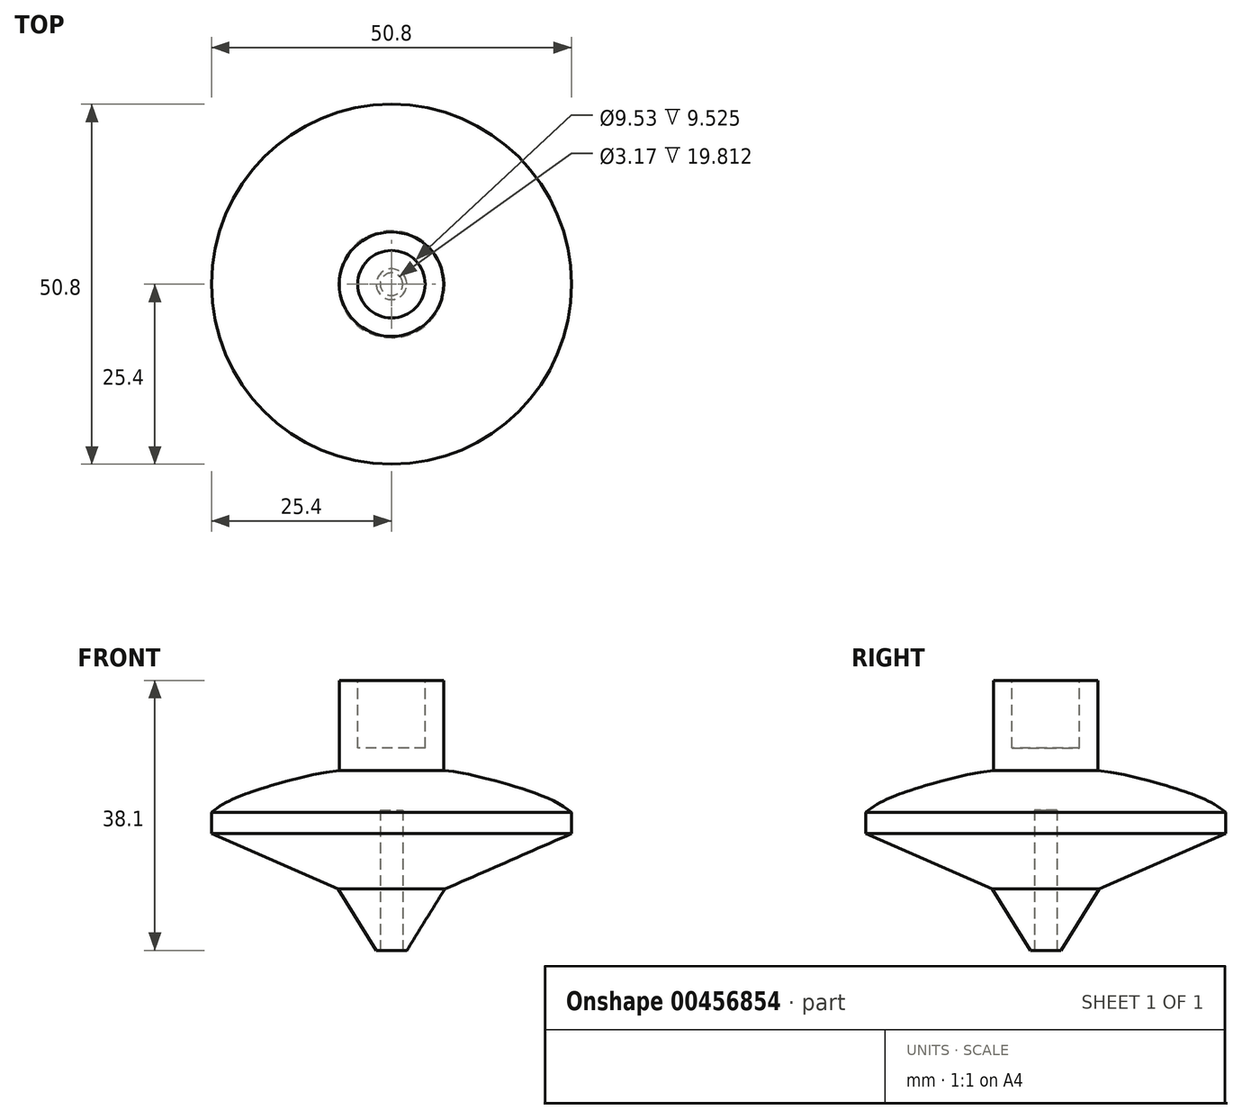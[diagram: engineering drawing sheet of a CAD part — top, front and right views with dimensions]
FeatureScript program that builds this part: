
annotation { "Feature Type Name" : "Feature", "Feature Type Description" : "" }
export const myFeature = defineFeature(function(context is Context, id is Id, definition is map)
    precondition{}
    {
        {
            var Q0;
            Q0=qCreatedBy(makeId("Front.planeOp"),FACE);
            var sketch = newSketch(context, id + "F0", { "sketchPlane" : qUnion([Q0])});
            skLineSegment(sketch, "E0", {"start": v(7.37, 25.4) * mm, "end": v(7.37, 38.1) * mm});
            skLineSegment(sketch, "E1", {"start": v(7.37, 38.1) * mm, "end": v(0, 38.1) * mm});
            skLineSegment(sketch, "E2", {"start": v(0, 38.1) * mm, "end": v(0, 0) * mm});
            skLineSegment(sketch, "E3", {"start": v(0, 0) * mm, "end": v(2.16, 0) * mm});
            skLineSegment(sketch, "E4", {"start": v(2.16, 0) * mm, "end": v(7.53, 8.66) * mm});
            skFitSpline(sketch, "E5", {"points": [v(7.37, 25.4) * mm, v(15.3, 23.74) * mm, v(25.4, 19.44) * mm], "startDerivative": vector(15.83, -1.77) * mm, "endDerivative": vector(10.5, -10.23) * mm});
            skLineSegment(sketch, "E6", {"start": v(25.4, 19.44) * mm, "end": v(25.4, 16.46) * mm});
            skLineSegment(sketch, "E7", {"start": v(25.4, 16.46) * mm, "end": v(7.53, 8.66) * mm});
            skSolve(sketch);
        }
        {
            var Q0;
            Q0 = qSketchRegion(id + "F0", true);
            var Q1;
            Q1=sQuery(id+"F0.wireOp",EDGE,"E2");
            var Q2;
            Q2=sQuery(id+"F0.wireOp",EDGE,"E2");
            revolve(context, id + "F1", {"entities" : qUnion([Q0]), "surfaceEntities" : qUnion([Q1]), "axis" : qUnion([Q2]), "revolveType" : RevolveType.FULL});
        }
        {
            var Q0;
            Q0=makeQuery(id+"F1.opRevolve","SWEPT_FACE",FACE,{"disambiguationData":[OSD([sQuery(id+"F0.wireOp",EDGE,"E1")])]});
            var sketch = newSketch(context, id + "F2", { "sketchPlane" : qUnion([Q0])});
            skCircle(sketch, "E8", {"center": v(0, 0) * mm, "radius": 4.76 * mm});
            skSolve(sketch);
        }
        {
            var Q0;
            Q0 = qSketchRegion(id + "F2", true);
            extrude(context, id + "F3", {"entities" : qUnion([Q0]), "operationType" : NewBodyOperationType.REMOVE, "oppositeDirection" : true, "depth" : 9.52 * mm});
        }
        {
            var Q0;
            Q0=makeQuery(id+"F1.opRevolve","SWEPT_FACE",FACE,{"disambiguationData":[OSD([sQuery(id+"F0.wireOp",EDGE,"E3")])]});
            var sketch = newSketch(context, id + "F4", { "sketchPlane" : qUnion([Q0])});
            skCircle(sketch, "E9", {"center": v(0, 0) * mm, "radius": 1.59 * mm});
            skSolve(sketch);
        }
        {
            var Q0;
            Q0=makeQuery(id+"F4.imprint","IMPRINT",FACE,{"disambiguationData":[TD([[makeQuery(id+"F4.imprint","IMPRINT",EDGE,{"derivedFrom":sQuery(id+"F4.wireOp",EDGE,"E9")}),1.0]])]});
            extrude(context, id + "F5", {"entities" : qUnion([Q0]), "operationType" : NewBodyOperationType.REMOVE, "oppositeDirection" : true, "depth" : 19.8 * mm});
        }
    });
